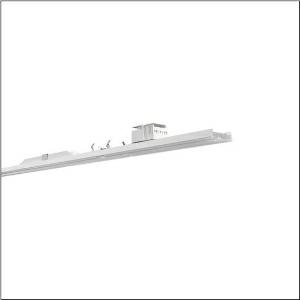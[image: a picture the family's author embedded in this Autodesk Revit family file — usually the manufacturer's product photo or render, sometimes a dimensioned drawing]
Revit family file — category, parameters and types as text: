
# Revit family: licross_r__11_recessed_ho_51tl12vv4gxl_a074
name_source: partatom
category: Lighting Fixtures
units: mm (PartAtom-declared; Revit-internal decimal feet)

## family parameters
Cut with Voids When Loaded = No
Host = Face
Light Source = No
Part Type = Normal
Room Calculation Point = No
Round Connector Dimension = Use Diameter
Shared = No

## types (1)
- --- (1 x LED, 16000 lm, 87.4 W, 4000K)
    Apparent Load = 87 VA
    CIE Flux Codes = 66 91 98 100 100
    Color Rendering = 80
    Color Temperature = 4000K
    Default Elevation = 1800 mm
    Description = Licross® 11 Recessed HOluminaire insert, length: 2.250mm, width: 66mm, height: 67mm, LED rated luminous flux: 16.000lm, light colour: 840, control gear: DALI 2, CLO, control gear: ECG DALI, with plug, 5-pole, with phase selection, mains connection: 220..240V, AC, 50/60Hz, halogen-free wiring, primary optical cover: cover, of PMMA, light emission: direct distribution, protection rating (complete): IP40, insulation class (complete): insulation class I (protective earthing), certification: CE, ENEC, VDE, UKCA, protection symbol: D if used in an environment without relevant dust loads with corresponding accessories, permissible ambient temperature for indoor applications: -25..+45°C, corresponds to IFS (International Featured Standards) requirements for safety and quality in the food industry, reducing of maximum allowable ambient temperature of 5°C with ceiling mounting, packaging unit: 1 piece
    Height = 58 mm
    Lamp = 1 x LED
    Lamp Light Flux = 16000 lm
    Lamp Power = 87.4 W
    Lamp count = 1
    Length = 2250 mm
    Luminous efficacy = 183 lm/W
    Manufacturer = Siteco
    ModVariant = No
    Model = 51TL12VV4GXL
    Mounting Place = Ceiling
    Mounting Type = Pendant
    Number of Poles = 1
    OnlyDefault = Yes
    Power Factor = 1
    Product Name = Licross® 11 Recessed HO
    Product group = luminaire insert
    ProductGroupID = 902
    Protection Class = Protection class I
    Protection Degree = IP 40
    RLX_Detail_Level = 1
    RlxData = <blob elided: 27317 chars, md5=9644d577>
    Socket = socket
    Standby Power = 0 W
    System Light Flux = 16000 lm
    System Power = 87 W
    Type Comments = factory setting: luminous flux: 100 % | dim-lin: 254 | 340 mA
    Type Image = l_1266722.jpg
    URL = http://relux.com
    VarID = @adj_129155
    Voltage = 0 V
    Weight = 0.00 kg
    Width = 66 mm

## geometry (parser evidence)
native form markers: Blend x4, Sweep x12
no freeform markers — native parametric forms only
